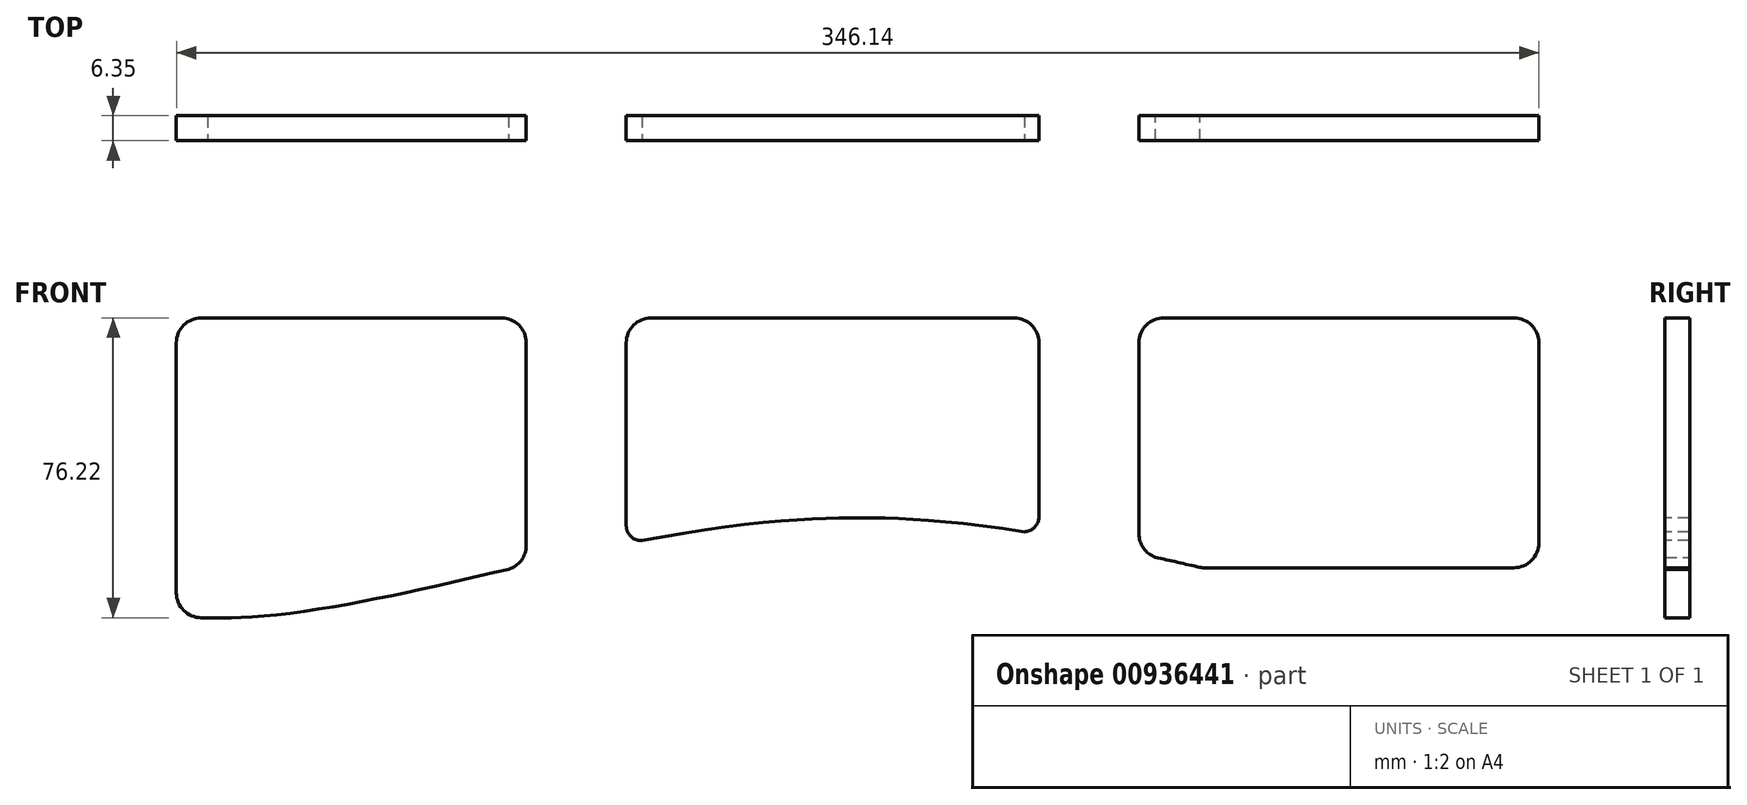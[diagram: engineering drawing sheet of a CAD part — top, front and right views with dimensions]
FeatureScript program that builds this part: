
annotation { "Feature Type Name" : "Feature", "Feature Type Description" : "" }
export const myFeature = defineFeature(function(context is Context, id is Id, definition is map)
    precondition{}
    {
        {
            var Q0;
            Q0=qCreatedBy(makeId("Front.planeOp"),FACE);
            var sketch = newSketch(context, id + "F0", { "sketchPlane" : qUnion([Q0])});
            skCircle(sketch, "E0", {"center": v(0, 0) * mm, "radius": 76.2 * mm, "construction": true});
            skLineSegment(sketch, "E1", {"start": v(0, 0) * mm, "end": v(381.07, 3.17) * mm, "construction": true});
            skCircle(sketch, "E2", {"center": v(381.07, 3.17) * mm, "radius": 76.2 * mm, "construction": true});
            skLineSegment(sketch, "E3", {"start": v(0, 0) * mm, "end": v(381.07, 0) * mm, "construction": true});
            skLineSegment(sketch, "E4", {"start": v(381.07, 0) * mm, "end": v(381.07, 3.17) * mm, "construction": true});
            skPoint(sketch, "E5", {"position": v(457.2, 0) * mm});
            skCircle(sketch, "E6", {"center": v(0, 0) * mm, "radius": 4.76 * mm});
            skCircle(sketch, "E7", {"center": v(381.07, 0) * mm, "radius": 4.76 * mm});
            skLineSegment(sketch, "E8", {"start": v(0, 88.9) * mm, "end": v(508, 88.9) * mm});
            skLineSegment(sketch, "E9", {"start": v(508, 88.9) * mm, "end": v(508, 44.45) * mm});
            skLineSegment(sketch, "E10", {"start": v(508, 44.45) * mm, "end": v(451.67, -22.68) * mm});
            skLineSegment(sketch, "E11", {"start": v(432.22, -31.75) * mm, "end": v(355.67, -31.75) * mm});
            skLineSegment(sketch, "E12", {"start": v(0, 88.9) * mm, "end": v(0, -76.2) * mm, "construction": true});
            skLineSegment(sketch, "E13", {"start": v(0, -31.75) * mm, "end": v(25.4, -31.75) * mm});
            skFitSpline(sketch, "E14", {"points": [v(25.4, -31.75) * mm, v(190.19, -6.35) * mm, v(355.67, -31.75) * mm], "startDerivative": vector(305.11, 0) * mm, "endDerivative": vector(304.49, 0) * mm});
            skPoint(sketch, "E15.visualSharp", {"position": v(444.06, -31.75) * mm});
            skArc(sketch, "E15.filletArc", {"start": v(432.22, -31.75) * mm, "mid": v(442.95, -29.37) * mm, "end": v(451.67, -22.68) * mm});
            skPoint(sketch, "E16", {"position": v(190.53, 1.59) * mm});
            skCircle(sketch, "E17.MirrorC", {"center": v(-381.07, 0) * mm, "radius": 4.76 * mm});
            skLineSegment(sketch, "E18.MirrorCS", {"start": v(-381.07, 0) * mm, "end": v(-381.07, 3.17) * mm, "construction": true});
            skArc(sketch, "E19.MirrorCS", {"start": v(-432.22, -31.75) * mm, "mid": v(-442.95, -29.37) * mm, "end": v(-451.67, -22.68) * mm});
            skLineSegment(sketch, "E20.MirrorCS", {"start": v(0, -31.75) * mm, "end": v(-25.4, -31.75) * mm});
            skPoint(sketch, "E21.MirrorP", {"position": v(-444.06, -31.75) * mm});
            skLineSegment(sketch, "E22.MirrorCS", {"start": v(-508, 88.9) * mm, "end": v(-508, 44.45) * mm});
            skPoint(sketch, "E23.MirrorP", {"position": v(-190.53, 1.59) * mm});
            skFitSpline(sketch, "E24.MirrorCS", {"points": [v(-25.4, -31.75) * mm, v(-190.19, -6.35) * mm, v(-355.67, -31.75) * mm], "startDerivative": vector(-305.11, 0) * mm, "endDerivative": vector(-304.49, 0) * mm});
            skLineSegment(sketch, "E25.MirrorCS", {"start": v(0, 0) * mm, "end": v(-381.07, 3.17) * mm, "construction": true});
            skLineSegment(sketch, "E26.MirrorCS", {"start": v(0, 0) * mm, "end": v(-381.07, 0) * mm, "construction": true});
            skCircle(sketch, "E27.MirrorC", {"center": v(-381.07, 3.17) * mm, "radius": 76.2 * mm, "construction": true});
            skLineSegment(sketch, "E28.MirrorCS", {"start": v(0, 88.9) * mm, "end": v(-508, 88.9) * mm});
            skPoint(sketch, "E29.MirrorP", {"position": v(-457.2, 0) * mm});
            skLineSegment(sketch, "E30.MirrorCS", {"start": v(-508, 44.45) * mm, "end": v(-451.67, -22.68) * mm});
            skLineSegment(sketch, "E31.MirrorCS", {"start": v(-432.22, -31.75) * mm, "end": v(-355.67, -31.75) * mm});
            skSolve(sketch);
        }
        {
            var Q0;
            Q0=makeQuery(id+"F0.imprint","IMPRINT",FACE,{"disambiguationData":[TD([[makeQuery(id+"F0.imprint","IMPRINT",EDGE,{"derivedFrom":sQuery(id+"F0.wireOp",EDGE,"E7")}),-1.0]])]});
            extrude(context, id + "F1", {"entities" : qUnion([Q0]), "depth" : 6.35 * mm, "offsetDistance" : 25.4 * mm});
        }
        {
            var Q0;
            Q0=makeQuery(id+"F1.opExtrude","CAP_FACE",FACE,{"disambiguationData":[OSD([sQuery(id+"F0.wireOp",EDGE,"E7"),sQuery(id+"F0.wireOp",EDGE,"E8"),sQuery(id+"F0.wireOp",EDGE,"E9"),sQuery(id+"F0.wireOp",EDGE,"E10"),sQuery(id+"F0.wireOp",EDGE,"E11"),sQuery(id+"F0.wireOp",EDGE,"E13"),sQuery(id+"F0.wireOp",EDGE,"E14"),sQuery(id+"F0.wireOp",EDGE,"E15.filletArc"),sQuery(id+"F0.wireOp",EDGE,"E6"),sQuery(id+"F0.wireOp",EDGE,"E17.MirrorC"),sQuery(id+"F0.wireOp",EDGE,"E19.MirrorCS"),sQuery(id+"F0.wireOp",EDGE,"E20.MirrorCS"),sQuery(id+"F0.wireOp",EDGE,"E22.MirrorCS"),sQuery(id+"F0.wireOp",EDGE,"E24.MirrorCS"),sQuery(id+"F0.wireOp",EDGE,"E28.MirrorCS"),sQuery(id+"F0.wireOp",EDGE,"E30.MirrorCS"),sQuery(id+"F0.wireOp",EDGE,"E31.MirrorCS")])],"isStart":false});
            var sketch = newSketch(context, id + "F2", { "sketchPlane" : qUnion([Q0])});
            skLineSegment(sketch, "E32", {"start": v(0, -31.75) * mm, "end": v(0, 88.9) * mm, "construction": true});
            skLineSegment(sketch, "E33.bottom", {"start": v(23.81, 63.5) * mm, "end": v(112.71, 63.5) * mm});
            skLineSegment(sketch, "E33.left", {"start": v(17.46, 57.15) * mm, "end": v(17.46, 6.35) * mm});
            skLineSegment(sketch, "E33.right", {"start": v(119.06, 57.15) * mm, "end": v(119.06, 8.63) * mm});
            skLineSegment(sketch, "E34.bottom", {"start": v(281.05, 63.5) * mm, "end": v(357.25, 63.5) * mm});
            skLineSegment(sketch, "E34.left", {"start": v(274.7, 57.15) * mm, "end": v(274.7, 5.7) * mm});
            skLineSegment(sketch, "E34.right", {"start": v(363.6, 57.15) * mm, "end": v(363.6, -6.35) * mm});
            skLineSegment(sketch, "E35", {"start": v(398.53, 57.15) * mm, "end": v(398.53, -6.35) * mm});
            skLineSegment(sketch, "E36", {"start": v(437.08, -10.43) * mm, "end": v(481.11, 42.05) * mm});
            skLineSegment(sketch, "E37", {"start": v(476.25, 63.5) * mm, "end": v(404.88, 63.5) * mm});
            skLineSegment(sketch, "E38", {"start": v(482.6, 57.15) * mm, "end": v(482.6, 46.13) * mm});
            skLineSegment(sketch, "E39", {"start": v(404.88, -12.7) * mm, "end": v(432.22, -12.7) * mm});
            skFitSpline(sketch, "E40.0", {"points": [v(25.4, -12.7) * mm, v(30.96, -12.7) * mm, v(42.53, -12) * mm, v(61.08, -9.23) * mm, v(80.66, -5.21) * mm, v(101.13, -0.5) * mm, v(118.84, 3.54) * mm, v(133.37, 6.5) * mm, v(144.44, 8.53) * mm, v(155.67, 10.26) * mm, v(165.18, 11.38) * mm, v(172.86, 12.05) * mm, v(178.66, 12.42) * mm, v(183.52, 12.6) * mm, v(187.43, 12.69) * mm, v(190.37, 12.7) * mm, v(193.31, 12.69) * mm, v(197.22, 12.6) * mm, v(202.08, 12.4) * mm, v(207.89, 12.03) * mm, v(215.57, 11.36) * mm, v(225.09, 10.24) * mm, v(236.35, 8.5) * mm, v(247.44, 6.49) * mm, v(262.01, 3.52) * mm, v(279.79, -0.5) * mm, v(300.33, -5.22) * mm, v(319.97, -9.24) * mm, v(338.56, -12) * mm, v(350.12, -12.7) * mm, v(355.67, -12.7) * mm]});
            skLineSegment(sketch, "E41", {"start": v(23.81, 0) * mm, "end": v(102.6, 0) * mm});
            skLineSegment(sketch, "E42", {"start": v(355.67, -12.7) * mm, "end": v(357.25, -12.7) * mm});
            skPoint(sketch, "E43.visualSharp", {"position": v(363.6, -12.7) * mm});
            skArc(sketch, "E43.filletArc", {"start": v(357.25, -12.7) * mm, "mid": v(361.74, -10.84) * mm, "end": v(363.6, -6.35) * mm});
            skLineSegment(sketch, "E44", {"start": v(144.46, 12.96) * mm, "end": v(144.46, 57.15) * mm});
            skLineSegment(sketch, "E45", {"start": v(150.81, 63.5) * mm, "end": v(242.95, 63.5) * mm});
            skLineSegment(sketch, "E46", {"start": v(249.3, 57.15) * mm, "end": v(249.3, 10.7) * mm});
            skFitSpline(sketch, "E47.trimOffspring", {"points": [v(25.4, -12.7) * mm, v(30.96, -12.7) * mm, v(42.53, -12) * mm, v(61.08, -9.23) * mm, v(80.66, -5.21) * mm, v(101.13, -0.5) * mm, v(118.84, 3.54) * mm, v(133.37, 6.5) * mm, v(144.44, 8.53) * mm, v(155.67, 10.26) * mm, v(165.18, 11.38) * mm, v(172.86, 12.05) * mm, v(178.66, 12.42) * mm, v(183.52, 12.6) * mm, v(187.43, 12.69) * mm, v(190.37, 12.7) * mm, v(193.31, 12.69) * mm, v(197.22, 12.6) * mm, v(202.08, 12.4) * mm, v(207.89, 12.03) * mm, v(215.57, 11.36) * mm, v(225.09, 10.24) * mm, v(236.35, 8.5) * mm, v(247.44, 6.49) * mm, v(262.01, 3.52) * mm, v(279.79, -0.5) * mm, v(300.33, -5.22) * mm, v(319.97, -9.24) * mm, v(338.56, -12) * mm, v(350.12, -12.7) * mm, v(355.67, -12.7) * mm]});
            skFitSpline(sketch, "E48.trimOffspring", {"points": [v(25.4, -12.7) * mm, v(30.96, -12.7) * mm, v(42.53, -12) * mm, v(61.08, -9.23) * mm, v(80.66, -5.21) * mm, v(101.13, -0.5) * mm, v(118.84, 3.54) * mm, v(133.37, 6.5) * mm, v(144.44, 8.53) * mm, v(155.67, 10.26) * mm, v(165.18, 11.38) * mm, v(172.86, 12.05) * mm, v(178.66, 12.42) * mm, v(183.52, 12.6) * mm, v(187.43, 12.69) * mm, v(190.37, 12.7) * mm, v(193.31, 12.69) * mm, v(197.22, 12.6) * mm, v(202.08, 12.4) * mm, v(207.89, 12.03) * mm, v(215.57, 11.36) * mm, v(225.09, 10.24) * mm, v(236.35, 8.5) * mm, v(247.44, 6.49) * mm, v(262.01, 3.52) * mm, v(279.79, -0.5) * mm, v(300.33, -5.22) * mm, v(319.97, -9.24) * mm, v(338.56, -12) * mm, v(350.12, -12.7) * mm, v(355.67, -12.7) * mm]});
            skPoint(sketch, "E49.visualSharp", {"position": v(17.46, 63.5) * mm});
            skArc(sketch, "E49.filletArc", {"start": v(23.81, 63.5) * mm, "mid": v(19.32, 61.64) * mm, "end": v(17.46, 57.15) * mm});
            skPoint(sketch, "E50.visualSharp", {"position": v(17.46, 0) * mm});
            skArc(sketch, "E50.filletArc", {"start": v(17.46, 6.35) * mm, "mid": v(19.32, 1.86) * mm, "end": v(23.81, 0) * mm});
            skPoint(sketch, "E51.visualSharp", {"position": v(119.06, 63.5) * mm});
            skArc(sketch, "E51.filletArc", {"start": v(119.06, 57.15) * mm, "mid": v(117.2, 61.64) * mm, "end": v(112.71, 63.5) * mm});
            skPoint(sketch, "E52.visualSharp", {"position": v(103.32, 0) * mm});
            skArc(sketch, "E52.filletArc", {"start": v(102.6, 0) * mm, "mid": v(103.31, 0.04) * mm, "end": v(104.02, 0.16) * mm});
            skPoint(sketch, "E53.visualSharp", {"position": v(119.06, 3.52) * mm});
            skArc(sketch, "E53.filletArc", {"start": v(114.09, 2.43) * mm, "mid": v(117.67, 4.66) * mm, "end": v(119.06, 8.63) * mm});
            skPoint(sketch, "E54.visualSharp", {"position": v(144.46, 8.48) * mm});
            skArc(sketch, "E54.filletArc", {"start": v(144.46, 12.96) * mm, "mid": v(145.8, 10.06) * mm, "end": v(148.86, 9.2) * mm});
            skPoint(sketch, "E55.visualSharp", {"position": v(249.3, 6.09) * mm});
            skArc(sketch, "E55.filletArc", {"start": v(244.8, 6.95) * mm, "mid": v(247.93, 7.77) * mm, "end": v(249.3, 10.7) * mm});
            skPoint(sketch, "E56.visualSharp", {"position": v(144.46, 63.5) * mm});
            skArc(sketch, "E56.filletArc", {"start": v(150.81, 63.5) * mm, "mid": v(146.32, 61.64) * mm, "end": v(144.46, 57.15) * mm});
            skPoint(sketch, "E57.visualSharp", {"position": v(249.3, 63.5) * mm});
            skArc(sketch, "E57.filletArc", {"start": v(249.3, 57.15) * mm, "mid": v(247.44, 61.64) * mm, "end": v(242.95, 63.5) * mm});
            skPoint(sketch, "E58.visualSharp", {"position": v(274.7, 63.5) * mm});
            skArc(sketch, "E58.filletArc", {"start": v(281.05, 63.5) * mm, "mid": v(276.56, 61.64) * mm, "end": v(274.7, 57.15) * mm});
            skPoint(sketch, "E59.visualSharp", {"position": v(363.6, 63.5) * mm});
            skArc(sketch, "E59.filletArc", {"start": v(363.6, 57.15) * mm, "mid": v(361.74, 61.64) * mm, "end": v(357.25, 63.5) * mm});
            skPoint(sketch, "E60.visualSharp", {"position": v(274.7, 0.64) * mm});
            skArc(sketch, "E60.filletArc", {"start": v(274.7, 5.7) * mm, "mid": v(276.09, 1.75) * mm, "end": v(279.64, -0.48) * mm});
            skPoint(sketch, "E61.visualSharp", {"position": v(398.53, 63.5) * mm});
            skArc(sketch, "E61.filletArc", {"start": v(404.88, 63.5) * mm, "mid": v(400.39, 61.64) * mm, "end": v(398.53, 57.15) * mm});
            skPoint(sketch, "E62.visualSharp", {"position": v(482.6, 63.5) * mm});
            skArc(sketch, "E62.filletArc", {"start": v(482.6, 57.15) * mm, "mid": v(480.74, 61.64) * mm, "end": v(476.25, 63.5) * mm});
            skPoint(sketch, "E63.visualSharp", {"position": v(482.6, 43.82) * mm});
            skArc(sketch, "E63.filletArc", {"start": v(481.11, 42.05) * mm, "mid": v(482.22, 43.96) * mm, "end": v(482.6, 46.13) * mm});
            skPoint(sketch, "E64.visualSharp", {"position": v(435.18, -12.7) * mm});
            skArc(sketch, "E64.filletArc", {"start": v(432.22, -12.7) * mm, "mid": v(434.9, -12.1) * mm, "end": v(437.08, -10.43) * mm});
            skPoint(sketch, "E65.visualSharp", {"position": v(398.53, -12.7) * mm});
            skArc(sketch, "E65.filletArc", {"start": v(398.53, -6.35) * mm, "mid": v(400.39, -10.84) * mm, "end": v(404.88, -12.7) * mm});
            skArc(sketch, "E66.MirrorCS", {"start": v(-102.6, 0) * mm, "mid": v(-103.31, 0.04) * mm, "end": v(-104.02, 0.16) * mm});
            skLineSegment(sketch, "E67.MirrorCS", {"start": v(-482.6, 57.15) * mm, "end": v(-482.6, 46.13) * mm});
            skArc(sketch, "E68.MirrorCS", {"start": v(-244.8, 6.95) * mm, "mid": v(-247.93, 7.77) * mm, "end": v(-249.3, 10.7) * mm});
            skArc(sketch, "E69.MirrorCS", {"start": v(-114.09, 2.43) * mm, "mid": v(-117.67, 4.66) * mm, "end": v(-119.06, 8.63) * mm});
            skArc(sketch, "E70.MirrorCS", {"start": v(-119.06, 57.15) * mm, "mid": v(-117.2, 61.64) * mm, "end": v(-112.71, 63.5) * mm});
            skArc(sketch, "E71.MirrorCS", {"start": v(-432.22, -12.7) * mm, "mid": v(-434.9, -12.1) * mm, "end": v(-437.08, -10.43) * mm});
            skArc(sketch, "E72.MirrorCS", {"start": v(-249.3, 57.15) * mm, "mid": v(-247.44, 61.64) * mm, "end": v(-242.95, 63.5) * mm});
            skArc(sketch, "E73.MirrorCS", {"start": v(-404.88, 63.5) * mm, "mid": v(-400.39, 61.64) * mm, "end": v(-398.53, 57.15) * mm});
            skArc(sketch, "E74.MirrorCS", {"start": v(-23.81, 63.5) * mm, "mid": v(-19.32, 61.64) * mm, "end": v(-17.46, 57.15) * mm});
            skArc(sketch, "E75.MirrorCS", {"start": v(-144.46, 12.96) * mm, "mid": v(-145.8, 10.06) * mm, "end": v(-148.86, 9.2) * mm});
            skArc(sketch, "E76.MirrorCS", {"start": v(-482.6, 57.15) * mm, "mid": v(-480.74, 61.64) * mm, "end": v(-476.25, 63.5) * mm});
            skArc(sketch, "E77.MirrorCS", {"start": v(-363.6, 57.15) * mm, "mid": v(-361.74, 61.64) * mm, "end": v(-357.25, 63.5) * mm});
            skArc(sketch, "E78.MirrorCS", {"start": v(-274.7, 5.7) * mm, "mid": v(-276.09, 1.75) * mm, "end": v(-279.64, -0.48) * mm});
            skArc(sketch, "E79.MirrorCS", {"start": v(-17.46, 6.35) * mm, "mid": v(-19.32, 1.86) * mm, "end": v(-23.81, 0) * mm});
            skArc(sketch, "E80.MirrorCS", {"start": v(-281.05, 63.5) * mm, "mid": v(-276.56, 61.64) * mm, "end": v(-274.7, 57.15) * mm});
            skArc(sketch, "E81.MirrorCS", {"start": v(-357.25, -12.7) * mm, "mid": v(-361.74, -10.84) * mm, "end": v(-363.6, -6.35) * mm});
            skArc(sketch, "E82.MirrorCS", {"start": v(-481.11, 42.05) * mm, "mid": v(-482.22, 43.96) * mm, "end": v(-482.6, 46.13) * mm});
            skArc(sketch, "E83.MirrorCS", {"start": v(-150.81, 63.5) * mm, "mid": v(-146.32, 61.64) * mm, "end": v(-144.46, 57.15) * mm});
            skArc(sketch, "E84.MirrorCS", {"start": v(-398.53, -6.35) * mm, "mid": v(-400.39, -10.84) * mm, "end": v(-404.88, -12.7) * mm});
            skLineSegment(sketch, "E85.MirrorCS", {"start": v(-355.67, -12.7) * mm, "end": v(-357.25, -12.7) * mm});
            skLineSegment(sketch, "E86.MirrorCS", {"start": v(-404.88, -12.7) * mm, "end": v(-432.22, -12.7) * mm});
            skLineSegment(sketch, "E87.MirrorCS", {"start": v(-363.6, 57.15) * mm, "end": v(-363.6, -6.35) * mm});
            skLineSegment(sketch, "E88.MirrorCS", {"start": v(-398.53, 57.15) * mm, "end": v(-398.53, -6.35) * mm});
            skLineSegment(sketch, "E89.MirrorCS", {"start": v(-437.08, -10.43) * mm, "end": v(-481.11, 42.05) * mm});
            skLineSegment(sketch, "E90.MirrorCS", {"start": v(-476.25, 63.5) * mm, "end": v(-404.88, 63.5) * mm});
            skPoint(sketch, "E91.MirrorP", {"position": v(-435.18, -12.7) * mm});
            skPoint(sketch, "E92.MirrorP", {"position": v(-144.46, 63.5) * mm});
            skLineSegment(sketch, "E93.MirrorCS", {"start": v(-150.81, 63.5) * mm, "end": v(-242.95, 63.5) * mm});
            skPoint(sketch, "E94.MirrorP", {"position": v(-482.6, 43.82) * mm});
            skPoint(sketch, "E95.MirrorP", {"position": v(-249.3, 6.09) * mm});
            skPoint(sketch, "E96.MirrorP", {"position": v(-482.6, 63.5) * mm});
            skLineSegment(sketch, "E97.MirrorCS", {"start": v(-281.05, 63.5) * mm, "end": v(-357.25, 63.5) * mm});
            skLineSegment(sketch, "E98.MirrorCS", {"start": v(-274.7, 57.15) * mm, "end": v(-274.7, 5.7) * mm});
            skPoint(sketch, "E99.MirrorP", {"position": v(-144.46, 8.48) * mm});
            skPoint(sketch, "E100.MirrorP", {"position": v(-398.53, -12.7) * mm});
            skLineSegment(sketch, "E101.MirrorCS", {"start": v(-23.81, 63.5) * mm, "end": v(-112.71, 63.5) * mm});
            skPoint(sketch, "E102.MirrorP", {"position": v(-274.7, 63.5) * mm});
            skLineSegment(sketch, "E103.MirrorCS", {"start": v(-23.81, 0) * mm, "end": v(-102.6, 0) * mm});
            skLineSegment(sketch, "E104.MirrorCS", {"start": v(-119.06, 57.15) * mm, "end": v(-119.06, 8.63) * mm});
            skLineSegment(sketch, "E105.MirrorCS", {"start": v(-144.46, 12.96) * mm, "end": v(-144.46, 57.15) * mm});
            skPoint(sketch, "E106.MirrorP", {"position": v(-17.46, 63.5) * mm});
            skPoint(sketch, "E107.MirrorP", {"position": v(-363.6, 63.5) * mm});
            skPoint(sketch, "E108.MirrorP", {"position": v(-17.46, 0) * mm});
            skPoint(sketch, "E109.MirrorP", {"position": v(-274.7, 0.64) * mm});
            skLineSegment(sketch, "E110.MirrorCS", {"start": v(-249.3, 57.15) * mm, "end": v(-249.3, 10.7) * mm});
            skPoint(sketch, "E111.MirrorP", {"position": v(-103.32, 0) * mm});
            skPoint(sketch, "E112.MirrorP", {"position": v(-249.3, 63.5) * mm});
            skPoint(sketch, "E113.MirrorP", {"position": v(-119.06, 63.5) * mm});
            skPoint(sketch, "E114.MirrorP", {"position": v(-119.06, 3.52) * mm});
            skPoint(sketch, "E115.MirrorP", {"position": v(-398.53, 63.5) * mm});
            skPoint(sketch, "E116.MirrorP", {"position": v(-363.6, -12.7) * mm});
            skLineSegment(sketch, "E117.MirrorCS", {"start": v(-17.46, 57.15) * mm, "end": v(-17.46, 6.35) * mm});
            skFitSpline(sketch, "E118.trimOffspring", {"points": [v(-25.4, -12.7) * mm, v(-30.96, -12.7) * mm, v(-42.53, -12) * mm, v(-61.08, -9.23) * mm, v(-80.66, -5.21) * mm, v(-101.13, -0.5) * mm, v(-118.84, 3.54) * mm, v(-133.37, 6.5) * mm, v(-144.44, 8.53) * mm, v(-155.67, 10.26) * mm, v(-165.18, 11.38) * mm, v(-172.86, 12.05) * mm, v(-178.66, 12.42) * mm, v(-183.52, 12.6) * mm, v(-187.43, 12.69) * mm, v(-190.37, 12.7) * mm, v(-193.31, 12.69) * mm, v(-197.22, 12.6) * mm, v(-202.08, 12.4) * mm, v(-207.89, 12.03) * mm, v(-215.57, 11.36) * mm, v(-225.09, 10.24) * mm, v(-236.35, 8.5) * mm, v(-247.44, 6.49) * mm, v(-262.01, 3.52) * mm, v(-279.79, -0.5) * mm, v(-300.33, -5.22) * mm, v(-319.97, -9.24) * mm, v(-338.56, -12) * mm, v(-350.12, -12.7) * mm, v(-355.67, -12.7) * mm]});
            skFitSpline(sketch, "E119.0", {"points": [v(-25.4, -12.7) * mm, v(-30.96, -12.7) * mm, v(-42.53, -12) * mm, v(-61.08, -9.23) * mm, v(-80.66, -5.21) * mm, v(-101.13, -0.5) * mm, v(-118.84, 3.54) * mm, v(-133.37, 6.5) * mm, v(-144.44, 8.53) * mm, v(-155.67, 10.26) * mm, v(-165.18, 11.38) * mm, v(-172.86, 12.05) * mm, v(-178.66, 12.42) * mm, v(-183.52, 12.6) * mm, v(-187.43, 12.69) * mm, v(-190.37, 12.7) * mm, v(-193.31, 12.69) * mm, v(-197.22, 12.6) * mm, v(-202.08, 12.4) * mm, v(-207.89, 12.03) * mm, v(-215.57, 11.36) * mm, v(-225.09, 10.24) * mm, v(-236.35, 8.5) * mm, v(-247.44, 6.49) * mm, v(-262.01, 3.52) * mm, v(-279.79, -0.5) * mm, v(-300.33, -5.22) * mm, v(-319.97, -9.24) * mm, v(-338.56, -12) * mm, v(-350.12, -12.7) * mm, v(-355.67, -12.7) * mm]});
            skFitSpline(sketch, "E120.trimOffspring", {"points": [v(-25.4, -12.7) * mm, v(-30.96, -12.7) * mm, v(-42.53, -12) * mm, v(-61.08, -9.23) * mm, v(-80.66, -5.21) * mm, v(-101.13, -0.5) * mm, v(-118.84, 3.54) * mm, v(-133.37, 6.5) * mm, v(-144.44, 8.53) * mm, v(-155.67, 10.26) * mm, v(-165.18, 11.38) * mm, v(-172.86, 12.05) * mm, v(-178.66, 12.42) * mm, v(-183.52, 12.6) * mm, v(-187.43, 12.69) * mm, v(-190.37, 12.7) * mm, v(-193.31, 12.69) * mm, v(-197.22, 12.6) * mm, v(-202.08, 12.4) * mm, v(-207.89, 12.03) * mm, v(-215.57, 11.36) * mm, v(-225.09, 10.24) * mm, v(-236.35, 8.5) * mm, v(-247.44, 6.49) * mm, v(-262.01, 3.52) * mm, v(-279.79, -0.5) * mm, v(-300.33, -5.22) * mm, v(-319.97, -9.24) * mm, v(-338.56, -12) * mm, v(-350.12, -12.7) * mm, v(-355.67, -12.7) * mm]});
            skFitSpline(sketch, "E121.trimOffspring", {"points": [v(-25.4, -12.7) * mm, v(-30.96, -12.7) * mm, v(-42.53, -12) * mm, v(-61.08, -9.23) * mm, v(-80.66, -5.21) * mm, v(-101.13, -0.5) * mm, v(-118.84, 3.54) * mm, v(-133.37, 6.5) * mm, v(-144.44, 8.53) * mm, v(-155.67, 10.26) * mm, v(-165.18, 11.38) * mm, v(-172.86, 12.05) * mm, v(-178.66, 12.42) * mm, v(-183.52, 12.6) * mm, v(-187.43, 12.69) * mm, v(-190.37, 12.7) * mm, v(-193.31, 12.69) * mm, v(-197.22, 12.6) * mm, v(-202.08, 12.4) * mm, v(-207.89, 12.03) * mm, v(-215.57, 11.36) * mm, v(-225.09, 10.24) * mm, v(-236.35, 8.5) * mm, v(-247.44, 6.49) * mm, v(-262.01, 3.52) * mm, v(-279.79, -0.5) * mm, v(-300.33, -5.22) * mm, v(-319.97, -9.24) * mm, v(-338.56, -12) * mm, v(-350.12, -12.7) * mm, v(-355.67, -12.7) * mm]});
            skSolve(sketch);
        }
        {
            var Q0;
            Q0=makeQuery(id+"F2.imprint","IMPRINT",FACE,{"disambiguationData":[TD([[makeQuery(id+"F2.imprint","IMPRINT",EDGE,{"derivedFrom":sQuery(id+"F2.wireOp",EDGE,"E67.MirrorCS")}),1.0]])]});
            var Q1;
            Q1=makeQuery(id+"F2.imprint","IMPRINT",FACE,{"disambiguationData":[TD([[makeQuery(id+"F2.imprint","IMPRINT",EDGE,{"derivedFrom":sQuery(id+"F2.wireOp",EDGE,"E77.MirrorCS")}),-1.0]])]});
            var Q2;
            Q2=makeQuery(id+"F2.imprint","IMPRINT",FACE,{"disambiguationData":[TD([[makeQuery(id+"F2.imprint","IMPRINT",EDGE,{"derivedFrom":sQuery(id+"F2.wireOp",EDGE,"E68.MirrorCS")}),-1.0]])]});
            var Q3;
            Q3=makeQuery(id+"F2.imprint","IMPRINT",FACE,{"disambiguationData":[TD([[makeQuery(id+"F2.imprint","IMPRINT",EDGE,{"derivedFrom":sQuery(id+"F2.wireOp",EDGE,"E66.MirrorCS")}),-1.0]])]});
            var Q4;
            Q4=makeQuery(id+"F2.imprint","IMPRINT",FACE,{"disambiguationData":[TD([[makeQuery(id+"F2.imprint","IMPRINT",EDGE,{"derivedFrom":sQuery(id+"F2.wireOp",EDGE,"E33.bottom")}),-1.0]])]});
            var Q5;
            Q5=makeQuery(id+"F2.imprint","IMPRINT",FACE,{"disambiguationData":[TD([[makeQuery(id+"F2.imprint","IMPRINT",EDGE,{"derivedFrom":sQuery(id+"F2.wireOp",EDGE,"E44")}),-1.0]])]});
            var Q6;
            Q6=makeQuery(id+"F2.imprint","IMPRINT",FACE,{"disambiguationData":[TD([[makeQuery(id+"F2.imprint","IMPRINT",EDGE,{"derivedFrom":sQuery(id+"F2.wireOp",EDGE,"E34.bottom")}),-1.0]])]});
            var Q7;
            Q7=makeQuery(id+"F2.imprint","IMPRINT",FACE,{"disambiguationData":[TD([[makeQuery(id+"F2.imprint","IMPRINT",EDGE,{"derivedFrom":sQuery(id+"F2.wireOp",EDGE,"E35")}),1.0]])]});
            extrude(context, id + "F3", {"entities" : qUnion([Q0, Q1, Q2, Q3, Q4, Q5, Q6, Q7]), "operationType" : NewBodyOperationType.REMOVE, "oppositeDirection" : true, "depth" : 25.4 * mm, "offsetDistance" : 25.4 * mm});
        }
    });
